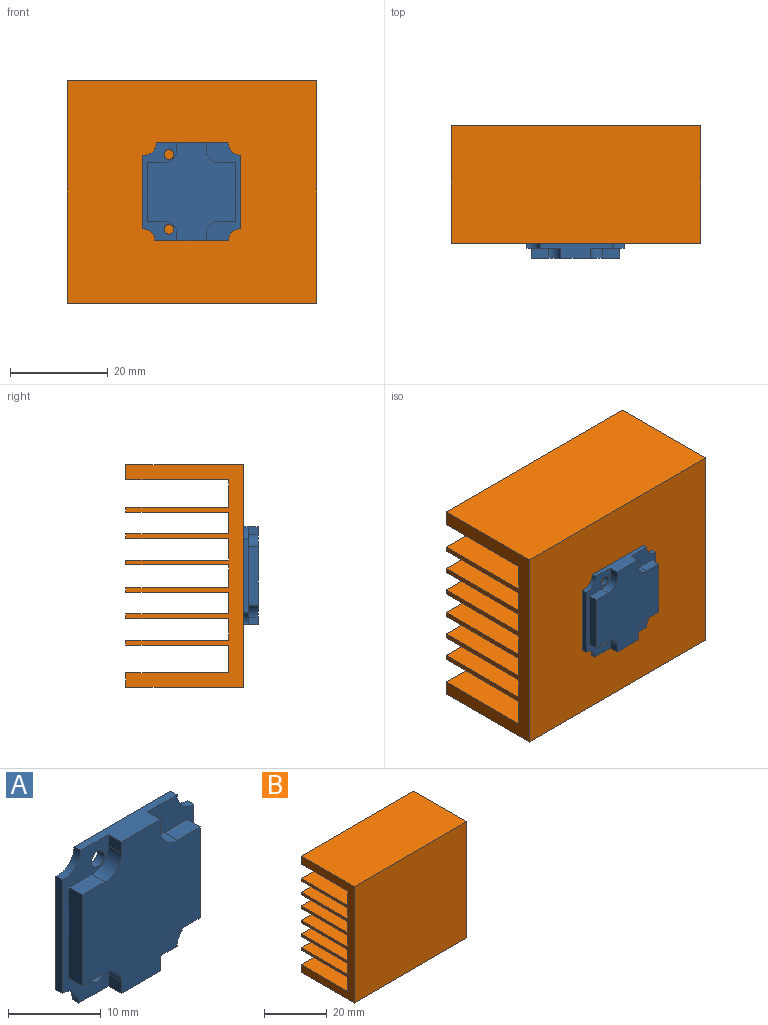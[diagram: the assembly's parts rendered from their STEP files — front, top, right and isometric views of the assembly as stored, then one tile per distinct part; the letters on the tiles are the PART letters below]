
ASSEMBLY  parts=2 mates=1
PART A: 28 faces, bbox 20x3x20 mm
  f0: cylinder r=2.5mm len=2.53mm, axis (0,1,0), area 7.9mm2, adj f1,f15,f16,f21
  f1: plane 2x1.48mm, normal (1,0,0), area 3mm2, adj f0,f2,f16,f21
  f2: plane 14.73x3mm, normal (0,0,1), area 26.7mm2, adj f1,f3,f16,f17,f20,f21,f22,f27
  f3: plane 2x1.5mm, normal (-1,0,0), area 3mm2, adj f2,f4,f16,f27
  f4: cylinder r=2.5mm len=2.5mm, axis (0,1,0), area 7.9mm2, adj f3,f5,f16,f27
  f5: plane 3.5x2mm, normal (0,0,1), area 7mm2, adj f4,f6,f16,f27
  f6: plane 12x2mm, normal (-1,0,0), area 24mm2, adj f5,f7,f16,f27
  f7: plane 3.5x2mm, normal (0,0,-1), area 7mm2, adj f6,f8,f16,f27
  f8: cylinder r=2.5mm len=2.5mm, axis (0,1,0), area 7.9mm2, adj f7,f9,f16,f27
  f9: plane 2x1.5mm, normal (-1,0,0), area 3mm2, adj f8,f10,f16,f27
  f10: plane 15x3mm, normal (0,0,-1), area 27mm2, adj f9,f11,f16,f17,f18,f21,f24,f27
  f11: plane 2x1.5mm, normal (1,0,0), area 3mm2, adj f10,f12,f16,f21
  f12: cylinder r=2.5mm len=2.5mm, axis (0,1,0), area 7.9mm2, adj f11,f13,f16,f21
  f13: plane 3.5x2mm, normal (0,0,-1), area 7mm2, adj f12,f14,f16,f21
  f14: plane 12x2mm, normal (1,0,0), area 24mm2, adj f13,f15,f16,f21
  f15: plane 3.5x2mm, normal (0,0,1), area 7mm2, adj f0,f14,f16,f21
  f16: plane 20x18mm, normal (0,-1,0), area 269.3mm2, adj f0,f1,f2,f3,f4,f5,f6,f7
  f17: plane 20x20mm, normal (0,1,0), area 373.4mm2, adj f2,f10,f18,f19,f20,f22,f23,f24
  f18: cylinder r=2.5mm len=2.5mm, axis (0,1,0), area 3.9mm2, adj f10,f17,f19,f21
  f19: plane 15x1mm, normal (1,0,0), area 15mm2, adj f17,f18,f20,f21
  f20: cylinder r=2.5mm len=2.5mm, axis (0,1,0), area 3.9mm2, adj f2,f17,f19,f21
  f21: plane 20x7mm, normal (0,-1,0), area 55.5mm2, adj f0,f1,f2,f10,f11,f12,f13,f14
  f22: cylinder r=2.5mm len=2.77mm, axis (0,1,0), area 4.2mm2, adj f2,f17,f23,f27
  f23: plane 15x1mm, normal (-1,0,0), area 15mm2, adj f17,f22,f24,f27
  f24: cylinder r=2.5mm len=2.5mm, axis (0,1,0), area 3.9mm2, adj f10,f17,f23,f27
  f25: cylinder r=1mm len=2mm, axis (0,1,0), area 6.3mm2, adj f17,f27
  f26: cylinder r=1mm len=2mm, axis (0,1,0), area 6.3mm2, adj f17,f27
  f27: plane 20x7mm, normal (0,-1,0), area 48.5mm2, adj f2,f3,f4,f5,f6,f7,f8,f9
PART B: 34 faces, bbox 51x24x45.5 mm
  f0: plane 51x3.04mm, normal (0,1,0), area 154.8mm2, adj f7,f9,f10,f32
  f1: plane 51x1mm, normal (0,1,0), area 51mm2, adj f7,f10,f13,f28
  f2: plane 51x1mm, normal (0,1,0), area 51mm2, adj f7,f10,f26,f29
  f3: plane 51x3.14mm, normal (0,1,0), area 159.9mm2, adj f7,f8,f10,f23
  f4: plane 51x1mm, normal (0,1,0), area 51mm2, adj f7,f10,f16,f20
  f5: plane 51x1mm, normal (0,1,0), area 51mm2, adj f7,f10,f17,f31
  f6: plane 51x1mm, normal (0,1,0), area 51mm2, adj f7,f10,f14,f19
  f7: plane 45.5x24mm, normal (-1,0,0), area 392.1mm2, adj f0,f1,f2,f3,f4,f5,f6,f8
  f8: plane 51x24mm, normal (0,0,1), area 1224mm2, adj f3,f7,f10,f12
  f9: plane 51x24mm, normal (0,0,-1), area 1224mm2, adj f0,f7,f10,f12
  f10: plane 45.5x24mm, normal (1,0,0), area 392.1mm2, adj f0,f1,f2,f3,f4,f5,f6,f8
  f11: plane 51x1mm, normal (0,1,0), area 51mm2, adj f7,f10,f22,f25
  f12: plane 51x45.5mm, normal (0,-1,0), area 2320.5mm2, adj f7,f8,f9,f10
  f13: plane 51x21mm, normal (0,0,-1), area 1071mm2, adj f1,f7,f10,f15
  f14: plane 51x21mm, normal (0,0,1), area 1071mm2, adj f6,f7,f10,f15
  f15: plane 51x4.63mm, normal (0,1,0), area 236.1mm2, adj f7,f10,f13,f14
  f16: plane 51x21mm, normal (0,0,-1), area 1071mm2, adj f4,f7,f10,f18
  f17: plane 51x21mm, normal (0,0,1), area 1071mm2, adj f5,f7,f10,f18
  f18: plane 51x4.36mm, normal (0,1,0), area 222.4mm2, adj f7,f10,f16,f17
  f19: plane 51x21mm, normal (0,0,-1), area 1071mm2, adj f6,f7,f10,f21
  f20: plane 51x21mm, normal (0,0,1), area 1071mm2, adj f4,f7,f10,f21
  f21: plane 51x4.36mm, normal (0,1,0), area 222.4mm2, adj f7,f10,f19,f20
  f22: plane 51x21mm, normal (0,0,1), area 1071mm2, adj f7,f10,f11,f24
  f23: plane 51x21mm, normal (0,0,-1), area 1071mm2, adj f3,f7,f10,f24
  f24: plane 51x5.63mm, normal (0,1,0), area 287.1mm2, adj f7,f10,f22,f23
  f25: plane 51x21mm, normal (0,0,-1), area 1071mm2, adj f7,f10,f11,f27
  f26: plane 51x21mm, normal (0,0,1), area 1071mm2, adj f2,f7,f10,f27
  f27: plane 51x4.36mm, normal (0,1,0), area 222.4mm2, adj f7,f10,f25,f26
  f28: plane 51x21mm, normal (0,0,1), area 1071mm2, adj f1,f7,f10,f30
  f29: plane 51x21mm, normal (0,0,-1), area 1071mm2, adj f2,f7,f10,f30
  f30: plane 51x4.36mm, normal (0,1,0), area 222.4mm2, adj f7,f10,f28,f29
  f31: plane 51x21mm, normal (0,0,-1), area 1071mm2, adj f5,f7,f10,f33
  f32: plane 51x21mm, normal (0,0,1), area 1071mm2, adj f0,f7,f10,f33
  f33: plane 51x5.63mm, normal (0,1,0), area 287.1mm2, adj f7,f10,f31,f32
PLACE A t=(-11.62,-1.42,5.69)mm
PLACE B t=(-11.27,-1.42,5.62)mm
MATE planar B.f12 <-> A.f17  axis (0,-1,0) through (-11.52,-1.42,5.67)mm
